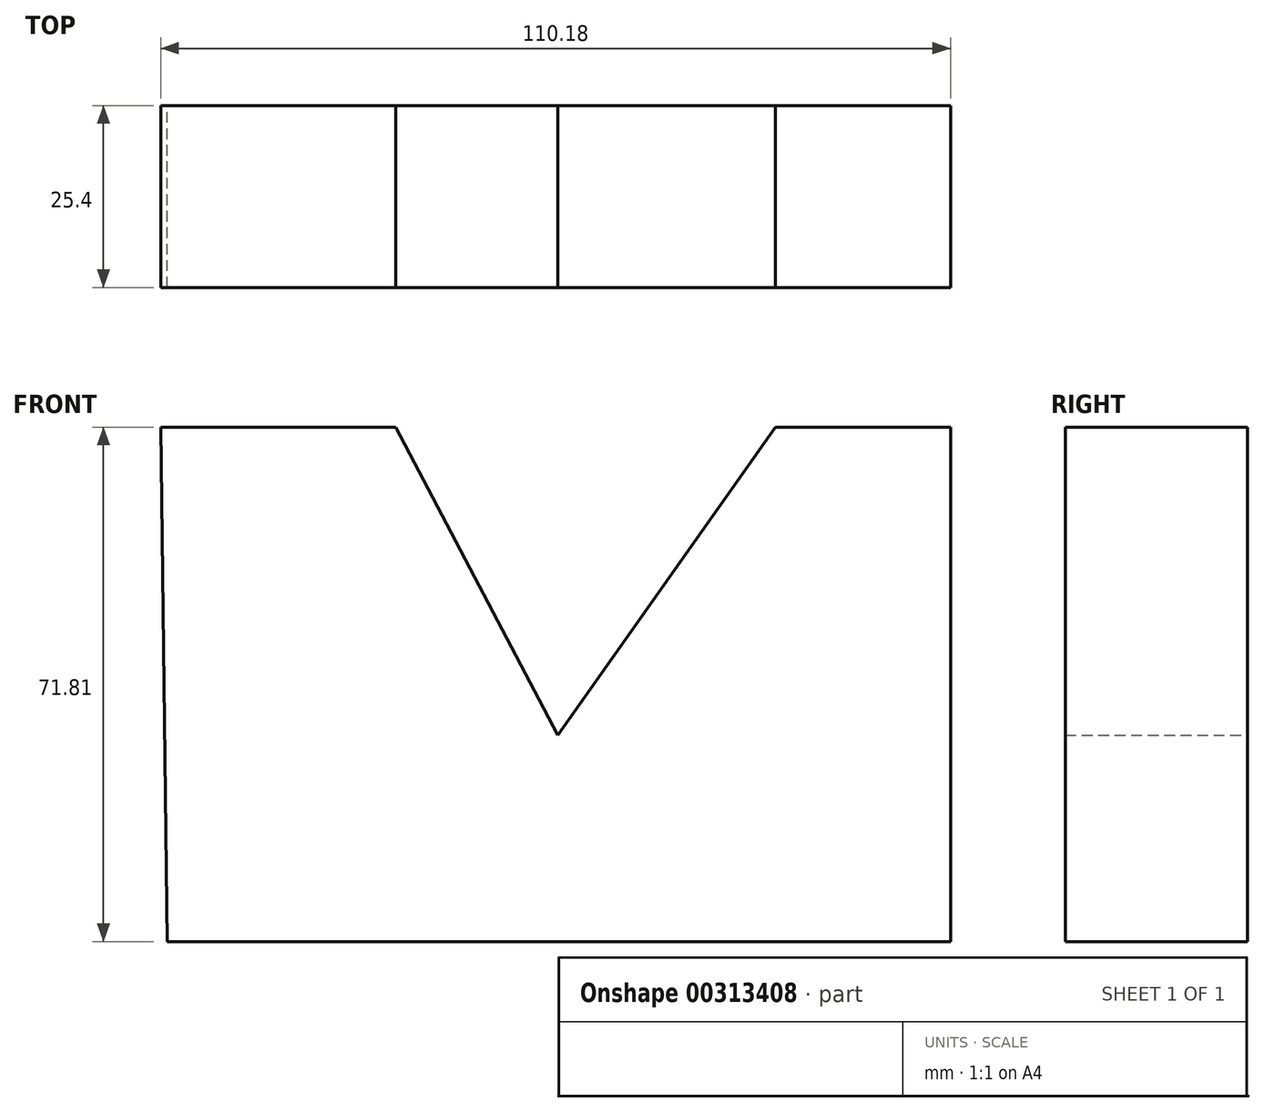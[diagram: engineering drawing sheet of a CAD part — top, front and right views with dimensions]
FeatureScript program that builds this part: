
annotation { "Feature Type Name" : "Feature", "Feature Type Description" : "" }
export const myFeature = defineFeature(function(context is Context, id is Id, definition is map)
    precondition{}
    {
        {
            var Q0;
            Q0=qCreatedBy(makeId("Front.planeOp"),FACE);
            var sketch = newSketch(context, id + "F0", { "sketchPlane" : qUnion([Q0])});
            skLineSegment(sketch, "E0", {"start": v(54.78, -42.56) * mm, "end": v(54.78, 29.25) * mm});
            skLineSegment(sketch, "E1", {"start": v(54.78, 29.25) * mm, "end": v(54.78, -42.56) * mm});
            skLineSegment(sketch, "E2", {"start": v(-54.47, -42.56) * mm, "end": v(54.78, -42.56) * mm});
            skLineSegment(sketch, "E3", {"start": v(54.78, 29.25) * mm, "end": v(30.33, 29.25) * mm});
            skLineSegment(sketch, "E4", {"start": v(30.33, 29.25) * mm, "end": v(0, -13.77) * mm});
            skLineSegment(sketch, "E5", {"start": v(0, -13.77) * mm, "end": v(-22.6, 29.25) * mm});
            skLineSegment(sketch, "E6", {"start": v(-22.6, 29.25) * mm, "end": v(-55.4, 29.25) * mm});
            skLineSegment(sketch, "E7", {"start": v(-55.4, 29.25) * mm, "end": v(-54.47, -42.56) * mm});
            skSolve(sketch);
        }
        {
            var Q0;
            Q0 = qSketchRegion(id + "F0", true);
            extrude(context, id + "F1", {"entities" : qUnion([Q0]), "depth" : 25.4 * mm});
        }
    });
